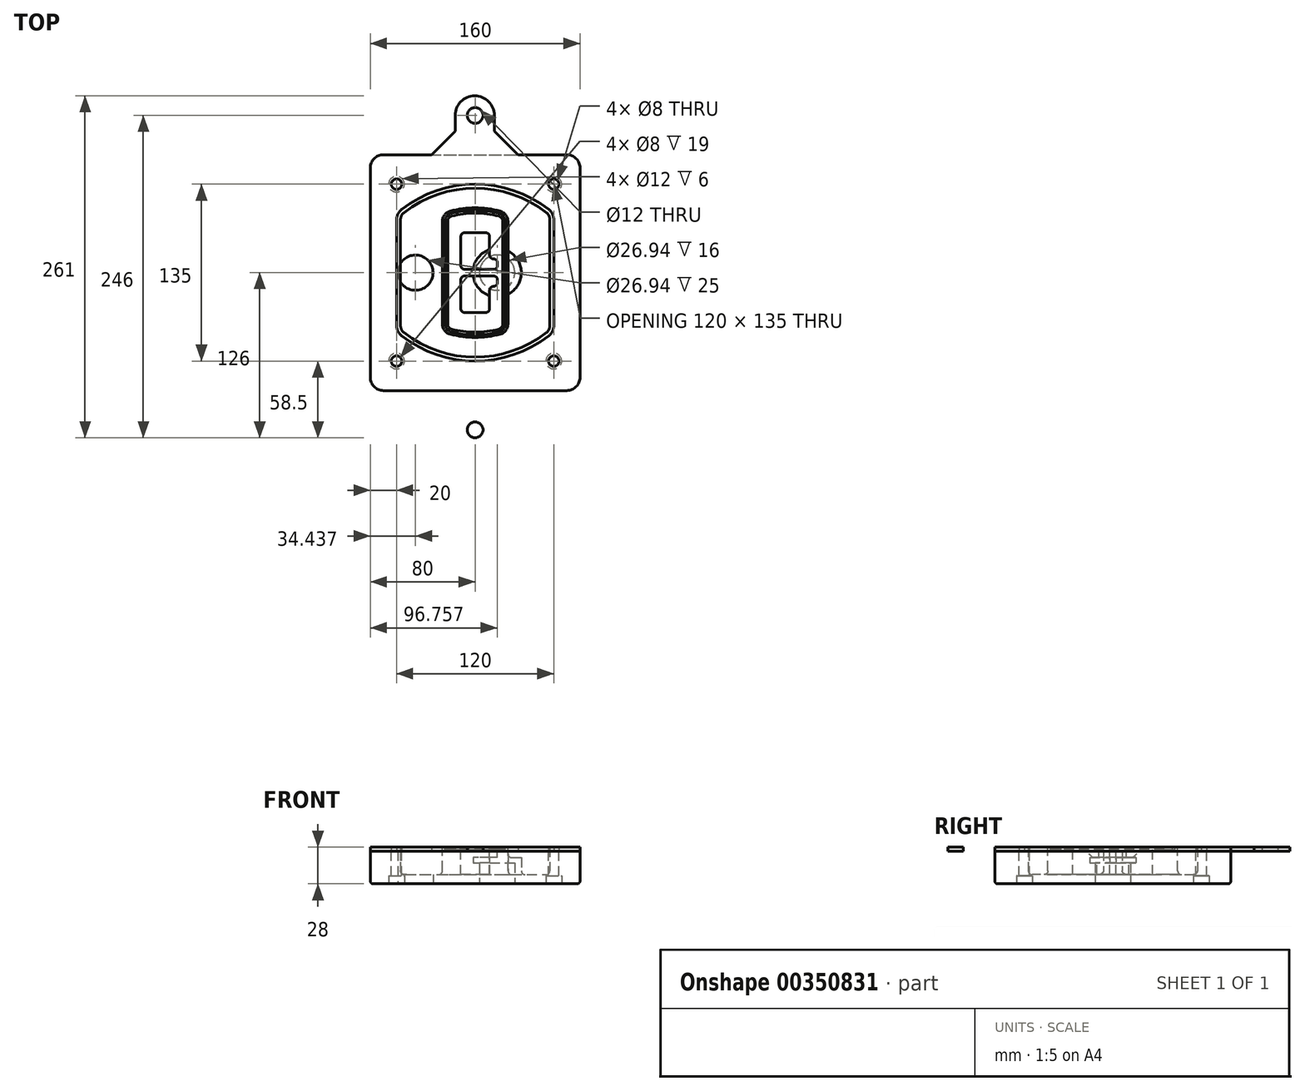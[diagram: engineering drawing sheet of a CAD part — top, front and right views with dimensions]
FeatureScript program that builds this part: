
annotation { "Feature Type Name" : "Feature", "Feature Type Description" : "" }
export const myFeature = defineFeature(function(context is Context, id is Id, definition is map)
    precondition{}
    {
        {
            var Q0;
            Q0=qCreatedBy(makeId("Top.planeOp"),FACE);
            var sketch = newSketch(context, id + "F0", { "sketchPlane" : qUnion([Q0])});
            skPoint(sketch, "E0.rect.middle", {"position": v(0, 0) * mm});
            skLineSegment(sketch, "E1.bottom", {"start": v(-70, -90) * mm, "end": v(70, -90) * mm});
            skLineSegment(sketch, "E1.top", {"start": v(-70, 90) * mm, "end": v(70, 90) * mm});
            skLineSegment(sketch, "E1.left", {"start": v(-80, -80) * mm, "end": v(-80, 80) * mm});
            skLineSegment(sketch, "E1.right", {"start": v(80, -80) * mm, "end": v(80, 80) * mm});
            skLineSegment(sketch, "E2", {"start": v(-80, 90) * mm, "end": v(80, -90) * mm, "construction": true});
            skLineSegment(sketch, "E3", {"start": v(80, 90) * mm, "end": v(-80, -90) * mm, "construction": true});
            skCircle(sketch, "E4", {"center": v(-60, 67.5) * mm, "radius": 4 * mm});
            skCircle(sketch, "E5", {"center": v(60, 67.5) * mm, "radius": 4 * mm});
            skCircle(sketch, "E6", {"center": v(60, -67.5) * mm, "radius": 4 * mm});
            skCircle(sketch, "E7", {"center": v(-60, -67.5) * mm, "radius": 4 * mm});
            skLineSegment(sketch, "E8", {"start": v(-60, 67.5) * mm, "end": v(60, 67.5) * mm, "construction": true});
            skLineSegment(sketch, "E9", {"start": v(60, 67.5) * mm, "end": v(60, -67.5) * mm, "construction": true});
            skLineSegment(sketch, "E10", {"start": v(60, -67.5) * mm, "end": v(-60, -67.5) * mm, "construction": true});
            skLineSegment(sketch, "E11", {"start": v(-60, -67.5) * mm, "end": v(-60, 67.5) * mm, "construction": true});
            skLineSegment(sketch, "E12", {"start": v(-60, 40.3) * mm, "end": v(-60, -40.3) * mm});
            skLineSegment(sketch, "E13", {"start": v(60, 40.3) * mm, "end": v(60, -40.3) * mm});
            skArc(sketch, "E14", {"start": v(56.15, 48.18) * mm, "mid": v(0, 67.5) * mm, "end": v(-56.15, 48.18) * mm});
            skArc(sketch, "E15", {"start": v(-56.15, -48.18) * mm, "mid": v(0, -67.5) * mm, "end": v(56.15, -48.18) * mm});
            skLineSegment(sketch, "E16", {"start": v(-60, 0) * mm, "end": v(60, 0) * mm, "construction": true});
            skPoint(sketch, "E17.visualSharp", {"position": v(-60, -45) * mm});
            skArc(sketch, "E17.filletArc", {"start": v(-60, -40.3) * mm, "mid": v(-58.99, -44.68) * mm, "end": v(-56.15, -48.18) * mm});
            skPoint(sketch, "E18.visualSharp", {"position": v(-60, 45) * mm});
            skArc(sketch, "E18.filletArc", {"start": v(-56.15, 48.18) * mm, "mid": v(-58.99, 44.68) * mm, "end": v(-60, 40.3) * mm});
            skPoint(sketch, "E19.visualSharp", {"position": v(60, 45) * mm});
            skArc(sketch, "E19.filletArc", {"start": v(60, 40.3) * mm, "mid": v(58.99, 44.68) * mm, "end": v(56.15, 48.18) * mm});
            skPoint(sketch, "E20.visualSharp", {"position": v(60, -45) * mm});
            skArc(sketch, "E20.filletArc", {"start": v(56.15, -48.18) * mm, "mid": v(58.99, -44.68) * mm, "end": v(60, -40.3) * mm});
            skPoint(sketch, "E21.visualSharp", {"position": v(-80, 90) * mm});
            skArc(sketch, "E21.filletArc", {"start": v(-70, 90) * mm, "mid": v(-77.07, 87.07) * mm, "end": v(-80, 80) * mm});
            skPoint(sketch, "E22.visualSharp", {"position": v(80, 90) * mm});
            skArc(sketch, "E22.filletArc", {"start": v(80, 80) * mm, "mid": v(77.07, 87.07) * mm, "end": v(70, 90) * mm});
            skPoint(sketch, "E23.visualSharp", {"position": v(80, -90) * mm});
            skArc(sketch, "E23.filletArc", {"start": v(70, -90) * mm, "mid": v(77.07, -87.07) * mm, "end": v(80, -80) * mm});
            skPoint(sketch, "E24.visualSharp", {"position": v(-80, -90) * mm});
            skArc(sketch, "E24.filletArc", {"start": v(-80, -80) * mm, "mid": v(-77.07, -87.07) * mm, "end": v(-70, -90) * mm});
            skArc(sketch, "E25.0", {"start": v(57, 40.3) * mm, "mid": v(56.3, 43.36) * mm, "end": v(54.3, 45.81) * mm});
            skLineSegment(sketch, "E25.1", {"start": v(57, 40.3) * mm, "end": v(57, -40.3) * mm});
            skArc(sketch, "E25.2", {"start": v(54.3, -45.81) * mm, "mid": v(56.3, -43.36) * mm, "end": v(57, -40.3) * mm});
            skArc(sketch, "E25.3", {"start": v(-54.3, -45.81) * mm, "mid": v(0, -64.5) * mm, "end": v(54.3, -45.81) * mm});
            skArc(sketch, "E25.4", {"start": v(-57, -40.3) * mm, "mid": v(-56.3, -43.36) * mm, "end": v(-54.3, -45.81) * mm});
            skArc(sketch, "E25.5", {"start": v(54.3, 45.81) * mm, "mid": v(0, 64.5) * mm, "end": v(-54.3, 45.81) * mm});
            skLineSegment(sketch, "E25.6", {"start": v(-57, 40.3) * mm, "end": v(-57, -40.3) * mm});
            skArc(sketch, "E25.7", {"start": v(-54.3, 45.81) * mm, "mid": v(-56.3, 43.36) * mm, "end": v(-57, 40.3) * mm});
            skArc(sketch, "E26.0", {"start": v(-58.62, 51.33) * mm, "mid": v(-62.58, 46.43) * mm, "end": v(-64, 40.3) * mm});
            skArc(sketch, "E26.1", {"start": v(58.62, 51.33) * mm, "mid": v(0, 71.5) * mm, "end": v(-58.62, 51.33) * mm});
            skArc(sketch, "E26.2", {"start": v(64, 40.3) * mm, "mid": v(62.58, 46.43) * mm, "end": v(58.62, 51.33) * mm});
            skLineSegment(sketch, "E26.3", {"start": v(64, 40.3) * mm, "end": v(64, -40.3) * mm});
            skArc(sketch, "E26.4", {"start": v(58.62, -51.33) * mm, "mid": v(62.58, -46.43) * mm, "end": v(64, -40.3) * mm});
            skLineSegment(sketch, "E26.5", {"start": v(-64, 40.3) * mm, "end": v(-64, -40.3) * mm});
            skArc(sketch, "E26.6", {"start": v(-58.62, -51.33) * mm, "mid": v(0, -71.5) * mm, "end": v(58.62, -51.33) * mm});
            skArc(sketch, "E26.7", {"start": v(-64, -40.3) * mm, "mid": v(-62.58, -46.43) * mm, "end": v(-58.62, -51.33) * mm});
            skSolve(sketch);
        }
        {
            var Q0;
            Q0=makeQuery(id+"F0.imprint","IMPRINT",FACE,{"disambiguationData":[TD([[makeQuery(id+"F0.imprint","IMPRINT",EDGE,{"derivedFrom":sQuery(id+"F0.wireOp",EDGE,"E1.bottom")}),1.0]])]});
            var Q1;
            Q1=makeQuery(id+"F0.imprint","IMPRINT",FACE,{"disambiguationData":[TD([[makeQuery(id+"F0.imprint","IMPRINT",EDGE,{"derivedFrom":sQuery(id+"F0.wireOp",EDGE,"E12")}),1.0]])]});
            var Q2;
            Q2=makeQuery(id+"F0.imprint","IMPRINT",FACE,{"disambiguationData":[TD([[makeQuery(id+"F0.imprint","IMPRINT",EDGE,{"derivedFrom":sQuery(id+"F0.wireOp",EDGE,"E25.0")}),1.0]])]});
            var Q3;
            Q3=makeQuery(id+"F0.imprint","IMPRINT",FACE,{"disambiguationData":[TD([[makeQuery(id+"F0.imprint","IMPRINT",EDGE,{"derivedFrom":sQuery(id+"F0.wireOp",EDGE,"E12")}),-1.0]])]});
            extrude(context, id + "F1", {"entities" : qUnion([Q0, Q1, Q2, Q3]), "oppositeDirection" : true, "depth" : 25 * mm});
        }
        {
            var Q0;
            Q0=makeQuery(id+"F0.imprint","IMPRINT",FACE,{"disambiguationData":[TD([[makeQuery(id+"F0.imprint","IMPRINT",EDGE,{"derivedFrom":sQuery(id+"F0.wireOp",EDGE,"E12")}),1.0]])]});
            extrude(context, id + "F2", {"entities" : qUnion([Q0]), "operationType" : NewBodyOperationType.ADD, "depth" : 3 * mm});
        }
        {
            var Q0;
            Q0=makeQuery(id+"F0.imprint","IMPRINT",FACE,{"disambiguationData":[TD([[makeQuery(id+"F0.imprint","IMPRINT",EDGE,{"derivedFrom":sQuery(id+"F0.wireOp",EDGE,"E25.0")}),1.0]])]});
            extrude(context, id + "F3", {"entities" : qUnion([Q0]), "operationType" : NewBodyOperationType.REMOVE, "oppositeDirection" : true, "depth" : 18 * mm});
        }
        {
            var Q0;
            Q0=makeQuery(id+"F2.opExtrude","CAP_FACE",FACE,{"disambiguationData":[OSD([sQuery(id+"F0.wireOp",EDGE,"E12"),sQuery(id+"F0.wireOp",EDGE,"E13"),sQuery(id+"F0.wireOp",EDGE,"E14"),sQuery(id+"F0.wireOp",EDGE,"E15"),sQuery(id+"F0.wireOp",EDGE,"E17.filletArc"),sQuery(id+"F0.wireOp",EDGE,"E18.filletArc"),sQuery(id+"F0.wireOp",EDGE,"E19.filletArc"),sQuery(id+"F0.wireOp",EDGE,"E20.filletArc"),sQuery(id+"F0.wireOp",EDGE,"E25.0"),sQuery(id+"F0.wireOp",EDGE,"E25.1"),sQuery(id+"F0.wireOp",EDGE,"E25.2"),sQuery(id+"F0.wireOp",EDGE,"E25.3"),sQuery(id+"F0.wireOp",EDGE,"E25.4"),sQuery(id+"F0.wireOp",EDGE,"E25.5"),sQuery(id+"F0.wireOp",EDGE,"E25.6"),sQuery(id+"F0.wireOp",EDGE,"E25.7")])],"isStart":false});
            var sketch = newSketch(context, id + "F4", { "sketchPlane" : qUnion([Q0])});
            skArc(sketch, "E27.0", {"start": v(-19.08, -46.97) * mm, "mid": v(0, -49.5) * mm, "end": v(19.08, -46.97) * mm});
            skArc(sketch, "E28.0", {"start": v(19.08, 46.97) * mm, "mid": v(0, 49.5) * mm, "end": v(-19.08, 46.97) * mm});
            skLineSegment(sketch, "E29", {"start": v(-25, 39.25) * mm, "end": v(-25, -39.25) * mm});
            skLineSegment(sketch, "E30", {"start": v(25, 39.25) * mm, "end": v(25, -39.25) * mm});
            skLineSegment(sketch, "E31", {"start": v(-25, 45.1) * mm, "end": v(25, 45.1) * mm, "construction": true});
            skLineSegment(sketch, "E32", {"start": v(-25, -45.1) * mm, "end": v(25, -45.1) * mm, "construction": true});
            skPoint(sketch, "E33.visualSharp", {"position": v(-25, 45.1) * mm});
            skArc(sketch, "E33.filletArc", {"start": v(-19.08, 46.97) * mm, "mid": v(-23.35, 44.11) * mm, "end": v(-25, 39.25) * mm});
            skPoint(sketch, "E34.visualSharp", {"position": v(25, 45.1) * mm});
            skArc(sketch, "E34.filletArc", {"start": v(25, 39.25) * mm, "mid": v(23.35, 44.11) * mm, "end": v(19.08, 46.97) * mm});
            skPoint(sketch, "E35.visualSharp", {"position": v(25, -45.1) * mm});
            skArc(sketch, "E35.filletArc", {"start": v(19.08, -46.97) * mm, "mid": v(23.35, -44.11) * mm, "end": v(25, -39.25) * mm});
            skPoint(sketch, "E36.visualSharp", {"position": v(-25, -45.1) * mm});
            skArc(sketch, "E36.filletArc", {"start": v(-25, -39.25) * mm, "mid": v(-23.35, -44.11) * mm, "end": v(-19.08, -46.97) * mm});
            skArc(sketch, "E37.0", {"start": v(54.3, 45.81) * mm, "mid": v(0, 64.5) * mm, "end": v(-54.3, 45.81) * mm});
            skArc(sketch, "E37.1", {"start": v(-54.3, 45.81) * mm, "mid": v(-56.3, 43.36) * mm, "end": v(-57, 40.3) * mm});
            skLineSegment(sketch, "E37.2", {"start": v(-57, 40.3) * mm, "end": v(-57, -40.3) * mm});
            skArc(sketch, "E37.3", {"start": v(-57, -40.3) * mm, "mid": v(-56.3, -43.36) * mm, "end": v(-54.3, -45.81) * mm});
            skArc(sketch, "E37.4", {"start": v(-54.3, -45.81) * mm, "mid": v(0, -64.5) * mm, "end": v(54.3, -45.81) * mm});
            skArc(sketch, "E37.5", {"start": v(54.3, -45.81) * mm, "mid": v(56.3, -43.36) * mm, "end": v(57, -40.3) * mm});
            skLineSegment(sketch, "E37.6", {"start": v(57, 40.3) * mm, "end": v(57, -40.3) * mm});
            skArc(sketch, "E37.7", {"start": v(57, 40.3) * mm, "mid": v(56.3, 43.36) * mm, "end": v(54.3, 45.81) * mm});
            skLineSegment(sketch, "E38.0", {"start": v(23, 39.25) * mm, "end": v(23, -39.25) * mm});
            skArc(sketch, "E38.1", {"start": v(18.56, -45.04) * mm, "mid": v(21.76, -42.9) * mm, "end": v(23, -39.25) * mm});
            skArc(sketch, "E38.2", {"start": v(-18.56, -45.04) * mm, "mid": v(0, -47.5) * mm, "end": v(18.56, -45.04) * mm});
            skArc(sketch, "E38.3", {"start": v(-23, -39.25) * mm, "mid": v(-21.76, -42.9) * mm, "end": v(-18.56, -45.04) * mm});
            skLineSegment(sketch, "E38.4", {"start": v(-23, 39.25) * mm, "end": v(-23, -39.25) * mm});
            skArc(sketch, "E38.5", {"start": v(23, 39.25) * mm, "mid": v(21.76, 42.9) * mm, "end": v(18.56, 45.04) * mm});
            skArc(sketch, "E38.6", {"start": v(-18.56, 45.04) * mm, "mid": v(-21.76, 42.9) * mm, "end": v(-23, 39.25) * mm});
            skArc(sketch, "E38.7", {"start": v(18.56, 45.04) * mm, "mid": v(0, 47.5) * mm, "end": v(-18.56, 45.04) * mm});
            skArc(sketch, "E39.0", {"start": v(21, 39.25) * mm, "mid": v(20.18, 41.68) * mm, "end": v(18.04, 43.1) * mm});
            skLineSegment(sketch, "E39.1", {"start": v(21, 39.25) * mm, "end": v(21, -39.25) * mm});
            skArc(sketch, "E39.2", {"start": v(18.04, -43.1) * mm, "mid": v(20.18, -41.68) * mm, "end": v(21, -39.25) * mm});
            skArc(sketch, "E39.3", {"start": v(-18.04, -43.1) * mm, "mid": v(0, -45.5) * mm, "end": v(18.04, -43.1) * mm});
            skArc(sketch, "E39.4", {"start": v(-21, -39.25) * mm, "mid": v(-20.18, -41.68) * mm, "end": v(-18.04, -43.1) * mm});
            skArc(sketch, "E39.5", {"start": v(18.04, 43.1) * mm, "mid": v(0, 45.5) * mm, "end": v(-18.04, 43.1) * mm});
            skLineSegment(sketch, "E39.6", {"start": v(-21, 39.25) * mm, "end": v(-21, -39.25) * mm});
            skArc(sketch, "E39.7", {"start": v(-18.04, 43.1) * mm, "mid": v(-20.18, 41.68) * mm, "end": v(-21, 39.25) * mm});
            skLineSegment(sketch, "E40", {"start": v(-25, 0) * mm, "end": v(25, 0) * mm, "construction": true});
            skLineSegment(sketch, "E41", {"start": v(-11, 5.5) * mm, "end": v(-11, 27.5) * mm});
            skLineSegment(sketch, "E42", {"start": v(-8, 30.5) * mm, "end": v(8, 30.5) * mm});
            skLineSegment(sketch, "E43", {"start": v(11, 27.5) * mm, "end": v(11, 13.5) * mm});
            skLineSegment(sketch, "E44", {"start": v(14, 10.5) * mm, "end": v(14, 10.5) * mm});
            skLineSegment(sketch, "E45", {"start": v(17, 7.5) * mm, "end": v(17, 5.5) * mm});
            skLineSegment(sketch, "E46", {"start": v(14, 2.5) * mm, "end": v(-8, 2.5) * mm});
            skPoint(sketch, "E47.visualSharp", {"position": v(-11, 30.5) * mm});
            skArc(sketch, "E47.filletArc", {"start": v(-8, 30.5) * mm, "mid": v(-10.12, 29.62) * mm, "end": v(-11, 27.5) * mm});
            skPoint(sketch, "E48.visualSharp", {"position": v(11, 30.5) * mm});
            skArc(sketch, "E48.filletArc", {"start": v(11, 27.5) * mm, "mid": v(10.12, 29.62) * mm, "end": v(8, 30.5) * mm});
            skPoint(sketch, "E49.visualSharp", {"position": v(11, 10.5) * mm});
            skArc(sketch, "E49.filletArc", {"start": v(11, 13.5) * mm, "mid": v(11.88, 11.38) * mm, "end": v(14, 10.5) * mm});
            skPoint(sketch, "E50.visualSharp", {"position": v(17, 10.5) * mm});
            skArc(sketch, "E50.filletArc", {"start": v(17, 7.5) * mm, "mid": v(16.12, 9.62) * mm, "end": v(14, 10.5) * mm});
            skPoint(sketch, "E51.visualSharp", {"position": v(17, 2.5) * mm});
            skArc(sketch, "E51.filletArc", {"start": v(14, 2.5) * mm, "mid": v(16.12, 3.38) * mm, "end": v(17, 5.5) * mm});
            skPoint(sketch, "E52.visualSharp", {"position": v(-11, 2.5) * mm});
            skArc(sketch, "E52.filletArc", {"start": v(-11, 5.5) * mm, "mid": v(-10.12, 3.38) * mm, "end": v(-8, 2.5) * mm});
            skLineSegment(sketch, "E53.0.MirrorCS", {"start": v(14, -2.5) * mm, "end": v(-8, -2.5) * mm});
            skArc(sketch, "E54.0.MirrorCS", {"start": v(-11, -5.5) * mm, "mid": v(-10.12, -3.38) * mm, "end": v(-8, -2.5) * mm});
            skLineSegment(sketch, "E55.0.MirrorCS", {"start": v(-11, -5.5) * mm, "end": v(-11, -27.5) * mm});
            skArc(sketch, "E56.0.MirrorCS", {"start": v(-8, -30.5) * mm, "mid": v(-10.12, -29.62) * mm, "end": v(-11, -27.5) * mm});
            skLineSegment(sketch, "E57.0.MirrorCS", {"start": v(-8, -30.5) * mm, "end": v(8, -30.5) * mm});
            skArc(sketch, "E58.0.MirrorCS", {"start": v(11, -27.5) * mm, "mid": v(10.12, -29.62) * mm, "end": v(8, -30.5) * mm});
            skLineSegment(sketch, "E59.0.MirrorCS", {"start": v(11, -27.5) * mm, "end": v(11, -13.5) * mm});
            skArc(sketch, "E60.0.MirrorCS", {"start": v(11, -13.5) * mm, "mid": v(11.88, -11.38) * mm, "end": v(14, -10.5) * mm});
            skArc(sketch, "E61.0.MirrorCS", {"start": v(17, -7.5) * mm, "mid": v(16.12, -9.62) * mm, "end": v(14, -10.5) * mm});
            skLineSegment(sketch, "E62.0.MirrorCS", {"start": v(17, -7.5) * mm, "end": v(17, -5.5) * mm});
            skArc(sketch, "E63.0.MirrorCS", {"start": v(14, -2.5) * mm, "mid": v(16.12, -3.38) * mm, "end": v(17, -5.5) * mm});
            skSolve(sketch);
        }
        {
            var Q0;
            Q0=makeQuery(id+"F4.imprint","IMPRINT",FACE,{"disambiguationData":[TD([[makeQuery(id+"F4.imprint","IMPRINT",EDGE,{"derivedFrom":sQuery(id+"F4.wireOp",EDGE,"E27.0")}),1.0]])]});
            var Q1;
            Q1=makeQuery(id+"F4.imprint","IMPRINT",FACE,{"disambiguationData":[TD([[makeQuery(id+"F4.imprint","IMPRINT",EDGE,{"derivedFrom":sQuery(id+"F4.wireOp",EDGE,"E38.0")}),-1.0]])]});
            var Q2;
            Q2=makeQuery(id+"F4.imprint","IMPRINT",FACE,{"disambiguationData":[TD([[makeQuery(id+"F4.imprint","IMPRINT",EDGE,{"derivedFrom":sQuery(id+"F4.wireOp",EDGE,"E39.0")}),1.0]])]});
            extrude(context, id + "F5", {"entities" : qUnion([Q0, Q1, Q2]), "operationType" : NewBodyOperationType.ADD, "endBound" : BoundingType.UP_TO_NEXT, "oppositeDirection" : true, "depth" : 25 * mm});
        }
        {
            var Q0;
            Q0=makeQuery(id+"F4.imprint","IMPRINT",FACE,{"disambiguationData":[TD([[makeQuery(id+"F4.imprint","IMPRINT",EDGE,{"derivedFrom":sQuery(id+"F4.wireOp",EDGE,"E38.0")}),-1.0]])]});
            extrude(context, id + "F6", {"entities" : qUnion([Q0]), "operationType" : NewBodyOperationType.REMOVE, "oppositeDirection" : true, "depth" : 2 * mm});
        }
        {
            var Q0;
            Q0=makeQuery(id+"F1.opExtrude","CAP_FACE",FACE,{"disambiguationData":[OSD([sQuery(id+"F0.wireOp",EDGE,"E1.bottom"),sQuery(id+"F0.wireOp",EDGE,"E1.top"),sQuery(id+"F0.wireOp",EDGE,"E1.left"),sQuery(id+"F0.wireOp",EDGE,"E1.right"),sQuery(id+"F0.wireOp",EDGE,"E4"),sQuery(id+"F0.wireOp",EDGE,"E5"),sQuery(id+"F0.wireOp",EDGE,"E6"),sQuery(id+"F0.wireOp",EDGE,"E7"),sQuery(id+"F0.wireOp",EDGE,"E21.filletArc"),sQuery(id+"F0.wireOp",EDGE,"E22.filletArc"),sQuery(id+"F0.wireOp",EDGE,"E23.filletArc"),sQuery(id+"F0.wireOp",EDGE,"E24.filletArc")])],"isStart":false});
            var sketch = newSketch(context, id + "F7", { "sketchPlane" : qUnion([Q0])});
            skCircle(sketch, "E64", {"center": v(16.76, 0) * mm, "radius": 13.47 * mm});
            skCircle(sketch, "E65", {"center": v(-45.56, 0) * mm, "radius": 13.47 * mm});
            skLineSegment(sketch, "E66", {"start": v(80, 0) * mm, "end": v(-80, 0) * mm});
            skCircle(sketch, "E67", {"center": v(16.76, 0) * mm, "radius": 18.47 * mm});
            skCircle(sketch, "E68", {"center": v(60, -67.5) * mm, "radius": 6 * mm});
            skCircle(sketch, "E69", {"center": v(-60, -67.5) * mm, "radius": 6 * mm});
            skCircle(sketch, "E70", {"center": v(-60, 67.5) * mm, "radius": 6 * mm});
            skCircle(sketch, "E71", {"center": v(60, 67.5) * mm, "radius": 6 * mm});
            skSolve(sketch);
        }
        {
            var Q0;
            {var subQ1=sQuery(id+"F7.wireOp",EDGE,"E66");var subQ4=sQuery(id+"F7.wireOp",EDGE,"E64");var subQ6=makeQuery(id+"F7.imprint","INTERSECT",VERTEX,{"disambiguationData":[OD(0.0)],"derivedFrom":[subQ4,subQ1]});Q0=makeQuery(id+"F7.imprint","IMPRINT",FACE,{"disambiguationData":[TD([[makeQuery(id+"F7.imprint","IMPRINT",EDGE,{"disambiguationData":[TD([[subQ6,-1.0]])],"derivedFrom":subQ4}),-1.0]])]});}
            var Q1;
            {var subQ0=sQuery(id+"F7.wireOp",EDGE,"E66");var subQ1=sQuery(id+"F7.wireOp",EDGE,"E64");var subQ3=makeQuery(id+"F7.imprint","INTERSECT",VERTEX,{"disambiguationData":[OD(0.0)],"derivedFrom":[subQ1,subQ0]});Q1=makeQuery(id+"F7.imprint","IMPRINT",FACE,{"disambiguationData":[TD([[makeQuery(id+"F7.imprint","IMPRINT",EDGE,{"disambiguationData":[TD([[subQ3,-1.0]])],"derivedFrom":subQ1}),1.0]])]});}
            var Q2;
            {var subQ0=sQuery(id+"F7.wireOp",EDGE,"E66");var subQ1=sQuery(id+"F7.wireOp",EDGE,"E64");var subQ3=makeQuery(id+"F7.imprint","INTERSECT",VERTEX,{"disambiguationData":[OD(0.0)],"derivedFrom":[subQ1,subQ0]});Q2=makeQuery(id+"F7.imprint","IMPRINT",FACE,{"disambiguationData":[TD([[makeQuery(id+"F7.imprint","IMPRINT",EDGE,{"disambiguationData":[TD([[subQ3,1.0]])],"derivedFrom":subQ1}),1.0]])]});}
            var Q3;
            {var subQ1=sQuery(id+"F7.wireOp",EDGE,"E66");var subQ4=sQuery(id+"F7.wireOp",EDGE,"E64");var subQ6=makeQuery(id+"F7.imprint","INTERSECT",VERTEX,{"disambiguationData":[OD(0.0)],"derivedFrom":[subQ4,subQ1]});Q3=makeQuery(id+"F7.imprint","IMPRINT",FACE,{"disambiguationData":[TD([[makeQuery(id+"F7.imprint","IMPRINT",EDGE,{"disambiguationData":[TD([[subQ6,1.0]])],"derivedFrom":subQ4}),-1.0]])]});}
            extrude(context, id + "F8", {"entities" : qUnion([Q0, Q1, Q2, Q3]), "operationType" : NewBodyOperationType.ADD, "oppositeDirection" : true, "depth" : 20 * mm});
        }
        {
            var Q0;
            {var subQ0=sQuery(id+"F7.wireOp",EDGE,"E66");var subQ1=sQuery(id+"F7.wireOp",EDGE,"E64");var subQ3=makeQuery(id+"F7.imprint","INTERSECT",VERTEX,{"disambiguationData":[OD(0.0)],"derivedFrom":[subQ1,subQ0]});Q0=makeQuery(id+"F7.imprint","IMPRINT",FACE,{"disambiguationData":[TD([[makeQuery(id+"F7.imprint","IMPRINT",EDGE,{"disambiguationData":[TD([[subQ3,-1.0]])],"derivedFrom":subQ1}),1.0]])]});}
            var Q1;
            {var subQ0=sQuery(id+"F7.wireOp",EDGE,"E66");var subQ1=sQuery(id+"F7.wireOp",EDGE,"E64");var subQ3=makeQuery(id+"F7.imprint","INTERSECT",VERTEX,{"disambiguationData":[OD(0.0)],"derivedFrom":[subQ1,subQ0]});Q1=makeQuery(id+"F7.imprint","IMPRINT",FACE,{"disambiguationData":[TD([[makeQuery(id+"F7.imprint","IMPRINT",EDGE,{"disambiguationData":[TD([[subQ3,1.0]])],"derivedFrom":subQ1}),1.0]])]});}
            extrude(context, id + "F9", {"entities" : qUnion([Q0, Q1]), "operationType" : NewBodyOperationType.REMOVE, "oppositeDirection" : true, "depth" : 16 * mm});
        }
        {
            var Q0;
            {var subQ0=sQuery(id+"F7.wireOp",EDGE,"E66");var subQ1=sQuery(id+"F7.wireOp",EDGE,"E65");var subQ3=makeQuery(id+"F7.imprint","INTERSECT",VERTEX,{"disambiguationData":[OD(0.0)],"derivedFrom":[subQ1,subQ0]});Q0=makeQuery(id+"F7.imprint","IMPRINT",FACE,{"disambiguationData":[TD([[makeQuery(id+"F7.imprint","IMPRINT",EDGE,{"disambiguationData":[TD([[subQ3,-1.0]])],"derivedFrom":subQ1}),1.0]])]});}
            var Q1;
            {var subQ0=sQuery(id+"F7.wireOp",EDGE,"E66");var subQ1=sQuery(id+"F7.wireOp",EDGE,"E65");var subQ3=makeQuery(id+"F7.imprint","INTERSECT",VERTEX,{"disambiguationData":[OD(0.0)],"derivedFrom":[subQ1,subQ0]});Q1=makeQuery(id+"F7.imprint","IMPRINT",FACE,{"disambiguationData":[TD([[makeQuery(id+"F7.imprint","IMPRINT",EDGE,{"disambiguationData":[TD([[subQ3,1.0]])],"derivedFrom":subQ1}),1.0]])]});}
            extrude(context, id + "F10", {"entities" : qUnion([Q0, Q1]), "operationType" : NewBodyOperationType.REMOVE, "oppositeDirection" : true, "depth" : 25 * mm});
        }
        {
            var Q0;
            Q0=makeQuery(id+"F7.imprint","IMPRINT",FACE,{"disambiguationData":[TD([[makeQuery(id+"F7.imprint","IMPRINT",EDGE,{"derivedFrom":sQuery(id+"F7.wireOp",EDGE,"E68")}),1.0]])]});
            var Q1;
            Q1=makeQuery(id+"F7.imprint","IMPRINT",FACE,{"disambiguationData":[TD([[makeQuery(id+"F7.imprint","IMPRINT",EDGE,{"derivedFrom":makeQuery(id+"F1.opExtrude","CAP_EDGE",EDGE,{"disambiguationData":[OSD([sQuery(id+"F0.wireOp",EDGE,"E5")])],"isStart":false})}),-1.0]])]});
            var Q2;
            Q2=makeQuery(id+"F7.imprint","IMPRINT",FACE,{"disambiguationData":[TD([[makeQuery(id+"F7.imprint","IMPRINT",EDGE,{"derivedFrom":sQuery(id+"F7.wireOp",EDGE,"E69")}),1.0]])]});
            var Q3;
            Q3=makeQuery(id+"F7.imprint","IMPRINT",FACE,{"disambiguationData":[TD([[makeQuery(id+"F7.imprint","IMPRINT",EDGE,{"derivedFrom":makeQuery(id+"F1.opExtrude","CAP_EDGE",EDGE,{"disambiguationData":[OSD([sQuery(id+"F0.wireOp",EDGE,"E4")])],"isStart":false})}),-1.0]])]});
            var Q4;
            Q4=makeQuery(id+"F7.imprint","IMPRINT",FACE,{"disambiguationData":[TD([[makeQuery(id+"F7.imprint","IMPRINT",EDGE,{"derivedFrom":sQuery(id+"F7.wireOp",EDGE,"E70")}),1.0]])]});
            var Q5;
            Q5=makeQuery(id+"F7.imprint","IMPRINT",FACE,{"disambiguationData":[TD([[makeQuery(id+"F7.imprint","IMPRINT",EDGE,{"derivedFrom":makeQuery(id+"F1.opExtrude","CAP_EDGE",EDGE,{"disambiguationData":[OSD([sQuery(id+"F0.wireOp",EDGE,"E7")])],"isStart":false})}),-1.0]])]});
            var Q6;
            Q6=makeQuery(id+"F7.imprint","IMPRINT",FACE,{"disambiguationData":[TD([[makeQuery(id+"F7.imprint","IMPRINT",EDGE,{"derivedFrom":sQuery(id+"F7.wireOp",EDGE,"E71")}),1.0]])]});
            var Q7;
            Q7=makeQuery(id+"F7.imprint","IMPRINT",FACE,{"disambiguationData":[TD([[makeQuery(id+"F7.imprint","IMPRINT",EDGE,{"derivedFrom":makeQuery(id+"F1.opExtrude","CAP_EDGE",EDGE,{"disambiguationData":[OSD([sQuery(id+"F0.wireOp",EDGE,"E6")])],"isStart":false})}),-1.0]])]});
            extrude(context, id + "F11", {"entities" : qUnion([Q0, Q1, Q2, Q3, Q4, Q5, Q6, Q7]), "operationType" : NewBodyOperationType.REMOVE, "oppositeDirection" : true, "depth" : 6 * mm});
        }
        {
            var Q0;
            Q0=makeQuery(id+"F9.boolean.opBoolean","COPY",FACE,{"derivedFrom":makeQuery(id+"F9.opExtrude","CAP_FACE",FACE,{"disambiguationData":[OSD([sQuery(id+"F7.wireOp",EDGE,"E64")])],"isStart":false})});
            var sketch = newSketch(context, id + "F12", { "sketchPlane" : qUnion([Q0])});
            skArc(sketch, "E72.0", {"start": v(11, 17.55) * mm, "mid": v(2.57, 11.82) * mm, "end": v(-1.54, 2.5) * mm});
            skArc(sketch, "E72.1", {"start": v(-1.54, -2.5) * mm, "mid": v(2.57, -11.82) * mm, "end": v(11, -17.55) * mm});
            skLineSegment(sketch, "E73", {"start": v(-1.54, -2.5) * mm, "end": v(14, -2.5) * mm});
            skLineSegment(sketch, "E74.0", {"start": v(14, 2.5) * mm, "end": v(-1.54, 2.5) * mm});
            skArc(sketch, "E74.1", {"start": v(14, 2.5) * mm, "mid": v(16.12, 3.38) * mm, "end": v(17, 5.5) * mm});
            skLineSegment(sketch, "E74.2", {"start": v(17, 7.5) * mm, "end": v(17, 5.5) * mm});
            skArc(sketch, "E74.3", {"start": v(17, 7.5) * mm, "mid": v(16.12, 9.62) * mm, "end": v(14, 10.5) * mm});
            skArc(sketch, "E74.4", {"start": v(11, 13.5) * mm, "mid": v(11.88, 11.38) * mm, "end": v(14, 10.5) * mm});
            skLineSegment(sketch, "E74.5", {"start": v(11, 17.55) * mm, "end": v(11, 13.5) * mm});
            skLineSegment(sketch, "E74.7", {"start": v(14, -2.5) * mm, "end": v(-1.54, -2.5) * mm});
            skArc(sketch, "E74.8", {"start": v(14, -2.5) * mm, "mid": v(16.12, -3.38) * mm, "end": v(17, -5.5) * mm});
            skLineSegment(sketch, "E74.9", {"start": v(17, -7.5) * mm, "end": v(17, -5.5) * mm});
            skArc(sketch, "E74.10", {"start": v(17, -7.5) * mm, "mid": v(16.12, -9.62) * mm, "end": v(14, -10.5) * mm});
            skArc(sketch, "E74.11", {"start": v(11, -13.5) * mm, "mid": v(11.88, -11.38) * mm, "end": v(14, -10.5) * mm});
            skLineSegment(sketch, "E74.12", {"start": v(11, -17.55) * mm, "end": v(11, -13.5) * mm});
            skPoint(sketch, "E75.orphan", {"position": v(11, -27.5) * mm});
            skPoint(sketch, "E76.orphan", {"position": v(-8, -2.5) * mm});
            skPoint(sketch, "E77.orphan", {"position": v(-8, 2.5) * mm});
            skPoint(sketch, "E78.orphan", {"position": v(11, 27.5) * mm});
            skSolve(sketch);
        }
        {
            var Q0;
            {var subQ7=sQuery(id+"F12.wireOp",EDGE,"E72.0");var subQ14=sQuery(id+"F12.wireOp",EDGE,"E72.1");var subQ16=sQuery(id+"F12.wireOp",EDGE,"E74.1");var subQ18=sQuery(id+"F12.wireOp",EDGE,"E74.8");Q0=qUnion([makeQuery(id+"F12.imprint","IMPRINT",FACE,{"disambiguationData":[TD([[makeQuery(id+"F12.imprint","IMPRINT",EDGE,{"derivedFrom":subQ7}),1.0]])]}),makeQuery(id+"F12.imprint","IMPRINT",FACE,{"disambiguationData":[TD([[makeQuery(id+"F12.imprint","IMPRINT",EDGE,{"derivedFrom":subQ14}),1.0]])]}),makeQuery(id+"F12.imprint","IMPRINT",FACE,{"disambiguationData":[TD([[makeQuery(id+"F12.imprint","IMPRINT",EDGE,{"derivedFrom":subQ16}),1.0]])]}),makeQuery(id+"F12.imprint","IMPRINT",FACE,{"disambiguationData":[TD([[makeQuery(id+"F12.imprint","IMPRINT",EDGE,{"derivedFrom":subQ18}),-1.0]])]})]);}
            var Q1;
            Q1=makeQuery(id+"F5.boolean.opBoolean","SPLIT",FACE,{"disambiguationData":[TD([makeQuery(id+"F5.opExtrude","SWEPT_FACE",FACE,{"disambiguationData":[OSD([sQuery(id+"F4.wireOp",EDGE,"E41")])]})])],"derivedFrom":makeQuery(id+"F3.boolean.opBoolean","COPY",FACE,{"derivedFrom":makeQuery(id+"F3.opExtrude","CAP_FACE",FACE,{"disambiguationData":[OSD([sQuery(id+"F0.wireOp",EDGE,"E25.0"),sQuery(id+"F0.wireOp",EDGE,"E25.1"),sQuery(id+"F0.wireOp",EDGE,"E25.2"),sQuery(id+"F0.wireOp",EDGE,"E25.3"),sQuery(id+"F0.wireOp",EDGE,"E25.4"),sQuery(id+"F0.wireOp",EDGE,"E25.5"),sQuery(id+"F0.wireOp",EDGE,"E25.6"),sQuery(id+"F0.wireOp",EDGE,"E25.7")])],"isStart":false})})});
            extrude(context, id + "F13", {"entities" : qUnion([Q0]), "operationType" : NewBodyOperationType.REMOVE, "endBound" : BoundingType.UP_TO_SURFACE, "endBoundEntityFace" : qUnion([Q1]), "depth" : 25 * mm});
        }
        {
            var Q0;
            Q0=makeQuery(id+"F3.boolean.opBoolean","COPY",EDGE,{"derivedFrom":makeQuery(id+"F3.opExtrude","CAP_EDGE",EDGE,{"disambiguationData":[OSD([sQuery(id+"F0.wireOp",EDGE,"E25.6")])],"isStart":false})});
            var Q1;
            Q1=makeQuery(id+"F8.boolean.opBoolean","INTERSECT",EDGE,{"derivedFrom":[makeQuery(id+"F5.opExtrude","SWEPT_FACE",FACE,{"disambiguationData":[OSD([sQuery(id+"F4.wireOp",EDGE,"E30")])]}),makeQuery(id+"F8.opExtrude","CAP_FACE",FACE,{"disambiguationData":[OSD([sQuery(id+"F7.wireOp",EDGE,"E67")])],"isStart":false})]});
            var Q2;
            Q2=makeQuery(id+"F8.boolean.opBoolean","INTERSECT",EDGE,{"disambiguationData":[OD(1.0)],"derivedFrom":[makeQuery(id+"F5.opExtrude","SWEPT_FACE",FACE,{"disambiguationData":[OSD([sQuery(id+"F4.wireOp",EDGE,"E30")])]}),makeQuery(id+"F8.opExtrude","SWEPT_FACE",FACE,{"disambiguationData":[OSD([sQuery(id+"F7.wireOp",EDGE,"E67")])]})]});
            var Q3;
            {var subQ0=sQuery(id+"F4.wireOp",EDGE,"E30");Q3=makeQuery(id+"F8.boolean.opBoolean","SPLIT",EDGE,{"disambiguationData":[TD([makeQuery(id+"F5.opExtrude","SWEPT_FACE",FACE,{"disambiguationData":[OSD([sQuery(id+"F4.wireOp",EDGE,"E35.filletArc")])]})])],"derivedFrom":makeQuery(id+"F5.opExtrude","CAP_EDGE",EDGE,{"disambiguationData":[OSD([subQ0])],"isStart":false})});}
            var Q4;
            {var subQ0=sQuery(id+"F0.wireOp",EDGE,"E25.7");var subQ1=sQuery(id+"F0.wireOp",EDGE,"E25.1");var subQ2=sQuery(id+"F0.wireOp",EDGE,"E25.6");var subQ3=sQuery(id+"F0.wireOp",EDGE,"E25.5");var subQ4=sQuery(id+"F0.wireOp",EDGE,"E25.4");var subQ5=sQuery(id+"F0.wireOp",EDGE,"E25.0");var subQ6=sQuery(id+"F0.wireOp",EDGE,"E25.2");var subQ7=sQuery(id+"F0.wireOp",EDGE,"E25.3");Q4=makeQuery(id+"F8.boolean.opBoolean","INTERSECT",EDGE,{"derivedFrom":[makeQuery(id+"F5.boolean.opBoolean","SPLIT",FACE,{"disambiguationData":[TD([makeQuery(id+"F2.opExtrude","SWEPT_FACE",FACE,{"disambiguationData":[OSD([subQ5])]})])],"derivedFrom":makeQuery(id+"F3.boolean.opBoolean","COPY",FACE,{"derivedFrom":makeQuery(id+"F3.opExtrude","CAP_FACE",FACE,{"disambiguationData":[OSD([subQ5,subQ1,subQ6,subQ7,subQ4,subQ3,subQ2,subQ0])],"isStart":false})})}),makeQuery(id+"F8.opExtrude","SWEPT_FACE",FACE,{"disambiguationData":[OSD([sQuery(id+"F7.wireOp",EDGE,"E67")])]})]});}
            var Q5;
            Q5=makeQuery(id+"F8.boolean.opBoolean","INTERSECT",EDGE,{"disambiguationData":[OD(0.0)],"derivedFrom":[makeQuery(id+"F5.opExtrude","SWEPT_FACE",FACE,{"disambiguationData":[OSD([sQuery(id+"F4.wireOp",EDGE,"E30")])]}),makeQuery(id+"F8.opExtrude","SWEPT_FACE",FACE,{"disambiguationData":[OSD([sQuery(id+"F7.wireOp",EDGE,"E67")])]})]});
            fillet(context, id + "F14", {"entities" : qUnion([Q0, Q1, Q2, Q3, Q4, Q5]), "radius" : 3 * mm, "tangentPropagation" : true, "allowEdgeOverflow" : false});
        }
        {
            var Q0;
            Q0=makeQuery(id+"F1.opExtrude","CAP_EDGE",EDGE,{"disambiguationData":[OSD([sQuery(id+"F0.wireOp",EDGE,"E1.bottom")])],"isStart":false});
            fillet(context, id + "F15", {"entities" : qUnion([Q0]), "radius" : 2 * mm, "tangentPropagation" : true, "allowEdgeOverflow" : false});
        }
        {
            var Q0;
            {var subQ0=sQuery(id+"F0.wireOp",EDGE,"E21.filletArc");var subQ1=sQuery(id+"F0.wireOp",EDGE,"E7");var subQ2=sQuery(id+"F0.wireOp",EDGE,"E6");var subQ3=sQuery(id+"F0.wireOp",EDGE,"E5");var subQ4=sQuery(id+"F0.wireOp",EDGE,"E4");var subQ5=sQuery(id+"F0.wireOp",EDGE,"E22.filletArc");var subQ6=sQuery(id+"F0.wireOp",EDGE,"E1.bottom");var subQ7=sQuery(id+"F0.wireOp",EDGE,"E1.right");var subQ8=sQuery(id+"F0.wireOp",EDGE,"E1.top");var subQ9=sQuery(id+"F0.wireOp",EDGE,"E1.left");var subQ10=sQuery(id+"F0.wireOp",EDGE,"E23.filletArc");var subQ11=sQuery(id+"F0.wireOp",EDGE,"E24.filletArc");Q0=makeQuery(id+"F2.boolean.opBoolean","SPLIT",FACE,{"disambiguationData":[TD([makeQuery(id+"F1.opExtrude","SWEPT_FACE",FACE,{"disambiguationData":[OSD([subQ6])]})])],"derivedFrom":makeQuery(id+"F1.opExtrude","CAP_FACE",FACE,{"disambiguationData":[OSD([subQ6,subQ8,subQ9,subQ7,subQ4,subQ3,subQ2,subQ1,subQ0,subQ5,subQ10,subQ11])],"isStart":true})});}
            var sketch = newSketch(context, id + "F16", { "sketchPlane" : qUnion([Q0])});
            skLineSegment(sketch, "E79", {"start": v(0, 90) * mm, "end": v(0, 120) * mm, "construction": true});
            skPoint(sketch, "E79.endSnap0", {"position": v(0, 90) * mm});
            skCircle(sketch, "E80", {"center": v(0, 120) * mm, "radius": 6 * mm});
            skLineSegment(sketch, "E81", {"start": v(-15.3, 120.71) * mm, "end": v(-15.3, 120) * mm});
            skArc(sketch, "E82", {"start": v(14.7, 120) * mm, "mid": v(-0.3, 135) * mm, "end": v(-15.3, 120) * mm});
            skLineSegment(sketch, "E83", {"start": v(14.7, 120.71) * mm, "end": v(14.7, 120) * mm});
            skLineSegment(sketch, "E84.MirrorCS", {"start": v(-15.3, -120.71) * mm, "end": v(-15.3, -120) * mm});
            skLineSegment(sketch, "E85.MirrorCS", {"start": v(14.7, -120.71) * mm, "end": v(14.7, -120) * mm});
            skLineSegment(sketch, "E86.MirrorCS", {"start": v(0, -90) * mm, "end": v(0, -120) * mm, "construction": true});
            skCircle(sketch, "E87.MirrorC", {"center": v(0, -120) * mm, "radius": 6 * mm});
            skLineSegment(sketch, "E88", {"start": v(-15.3, 108) * mm, "end": v(-33.3, 90) * mm});
            skLineSegment(sketch, "E89", {"start": v(14.7, 108) * mm, "end": v(32.7, 90) * mm});
            skLineSegment(sketch, "E90", {"start": v(-15.3, 120.71) * mm, "end": v(-15.3, 108) * mm});
            skLineSegment(sketch, "E91", {"start": v(14.7, 120) * mm, "end": v(14.7, 108) * mm});
            skLineSegment(sketch, "E92.MirrorCS", {"start": v(-15.3, -108) * mm, "end": v(-33.3, -90) * mm});
            skLineSegment(sketch, "E93.MirrorCS", {"start": v(-15.3, -120.71) * mm, "end": v(-15.3, -108) * mm});
            skArc(sketch, "E94.MirrorCS", {"start": v(14.7, -120) * mm, "mid": v(-0.3, -135) * mm, "end": v(-15.3, -120) * mm});
            skLineSegment(sketch, "E95.MirrorCS", {"start": v(14.7, -120) * mm, "end": v(14.7, -108) * mm});
            skLineSegment(sketch, "E96.MirrorCS", {"start": v(14.7, -108) * mm, "end": v(32.7, -90) * mm});
            skSolve(sketch);
        }
        {
            var Q0;
            Q0=makeQuery(id+"F16.imprint","IMPRINT",FACE,{"disambiguationData":[TD([[makeQuery(id+"F16.imprint","IMPRINT",EDGE,{"derivedFrom":makeQuery(id+"F1.opExtrude","CAP_EDGE",EDGE,{"disambiguationData":[OSD([sQuery(id+"F0.wireOp",EDGE,"E1.left")])],"isStart":true})}),-1.0]])]});
            var Q1;
            Q1=makeQuery(id+"F16.imprint","IMPRINT",FACE,{"disambiguationData":[TD([[makeQuery(id+"F16.imprint","IMPRINT",EDGE,{"derivedFrom":sQuery(id+"F16.wireOp",EDGE,"E80")}),-1.0]])]});
            var Q2;
            Q2=makeQuery(id+"F16.imprint","IMPRINT",FACE,{"disambiguationData":[TD([[makeQuery(id+"F16.imprint","IMPRINT",EDGE,{"derivedFrom":sQuery(id+"F16.wireOp",EDGE,"E87.MirrorC")}),1.0]])]});
            var Q3;
            Q3=makeQuery(id+"F2.opExtrude","CAP_FACE",FACE,{"disambiguationData":[OSD([sQuery(id+"F0.wireOp",EDGE,"E12"),sQuery(id+"F0.wireOp",EDGE,"E13"),sQuery(id+"F0.wireOp",EDGE,"E14"),sQuery(id+"F0.wireOp",EDGE,"E15"),sQuery(id+"F0.wireOp",EDGE,"E17.filletArc"),sQuery(id+"F0.wireOp",EDGE,"E18.filletArc"),sQuery(id+"F0.wireOp",EDGE,"E19.filletArc"),sQuery(id+"F0.wireOp",EDGE,"E20.filletArc"),sQuery(id+"F0.wireOp",EDGE,"E25.0"),sQuery(id+"F0.wireOp",EDGE,"E25.1"),sQuery(id+"F0.wireOp",EDGE,"E25.2"),sQuery(id+"F0.wireOp",EDGE,"E25.3"),sQuery(id+"F0.wireOp",EDGE,"E25.4"),sQuery(id+"F0.wireOp",EDGE,"E25.5"),sQuery(id+"F0.wireOp",EDGE,"E25.6"),sQuery(id+"F0.wireOp",EDGE,"E25.7")])],"isStart":false});
            extrude(context, id + "F17", {"entities" : qUnion([Q0, Q1, Q2]), "endBound" : BoundingType.UP_TO_SURFACE, "endBoundEntityFace" : qUnion([Q3]), "depth" : 3 * mm});
        }
    });
